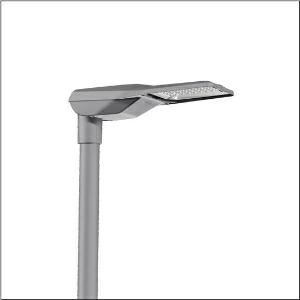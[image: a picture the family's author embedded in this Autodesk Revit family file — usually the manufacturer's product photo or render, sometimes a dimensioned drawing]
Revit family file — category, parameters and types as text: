
# Revit family: streetlight_sl_21_iq_mini___stw1_0a_5xe2e21d08hb_2a42
name_source: partatom
category: Lighting Fixtures
units: mm (PartAtom-declared; Revit-internal decimal feet)

## family parameters
Cut with Voids When Loaded = No
Host = Face
Light Source = No
Part Type = Normal
Room Calculation Point = No
Round Connector Dimension = Use Diameter
Shared = No

## types (1)
- --- (1 x LED, 7830 lm, 70.9 W, 2200K)
    Apparent Load = 71 VA
    CIE Flux Codes = 38 75 98 100 100
    Color Rendering = 70
    Color Temperature = 2200K
    Default Elevation = 1800 mm
    Description = Streetlight SL 21 iQ mini, mast luminaire, primary light control with lens, of PMMA, primary optical cover: cover, of toughened safety glass, transparent, light distribution: STW1.0a, light emission: direct distribution, primary light characteristic: asymmetric, installation type: post-top, side-entry, LED, High Power LED, rated luminous flux: 7.830lm, luminous efficacy: 110lm/W, light colour: 722, colour temperature: 2200K, control: Auto-Match, Temp-Guard, Lumen-Switch, Night-Set, Smart-Wire, Light-Fading, Desk-Remote (wireless, voltage-free reading and setting of iQ features in the workshop via application-optimized NFC function/RFID function), optimised constant luminous flux control (CLO 2.0), pre-setting: linear dimming characteristic, mains connection: 220..240V, AC, 50/60Hz, start of lifetime: 71W, end of service life: 75W, reduction: 31W, luminaire housing, of diecast aluminium, powder-coated, Siteco® metallic grey (DB 702S), corrosivity category C5 mid according to DIN EN ISO 12944, please order mast flange separately, inclination adjustable: 0°, 5°, 10°, 15°, sealing non-destructively replaceable, multi-level sealing system, length: 628mm, width: 235mm, height: 110mm, mast flange for spigot size: 42mm (side-entry): 5XC10008XM4, 60/48mm (side-entry/post-top): 5XC10108XM2, 76/60mm (side-entry/post-top): 5XC10108XM1, protection rating (complete): IP66, insulation class (complete): insulation class II (safety insulation), certification: CE, ENEC, ENEC+, VDE, impact resistance: IK09, permissible operating ambient temperature for outdoor applications: -40..+50°C, standard-compliant lighting for roads and squares, packaging unit: 1 piece

Light Distribution: STW1.0a
    Height = 110 mm
    Lamp = 1 x LED
    Lamp Light Flux = 7830 lm
    Lamp Power = 70.9 W
    Lamp count = 1
    Length = 625 mm
    Luminous efficacy = 110 lm/W
    Manufacturer = Siteco
    ModVariant = No
    Model = 5XE2E21D08HB
    Number of Poles = 1
    OnlyDefault = Yes
    Power Factor = 1
    Product Name = Streetlight SL 21 iQ mini | STW1.0a
    Product group = mast luminaire | pylon top
    ProductGroupID = 6100
    Protection Class = Protection class II
    Protection Degree = IP 66
    RLX_Detail_Level = 1
    RLX_Emergency_Light_Flux = 0 lm
    RLX_Emergency_Type = 0
    RLX_Emergency_Type_DB = No
    RlxData = <blob elided: 92489 chars, md5=6177a4c7>
    Socket = socket
    Standby Power = 0 W
    System Light Flux = 7830 lm
    System Power = 71 W
    Type Comments = factory setting: luminous flux: 100 % | dim-lin: 254 | 711 mA
    Type Image = l_1003519.jpg
    URL = http://relux.com
    VarID = @adj_128369
    Voltage = 0 V
    Weight = 0.00 kg
    Width = 234 mm

## geometry (parser evidence)
native form markers: Blend x4, Sweep x13
no freeform markers — native parametric forms only
